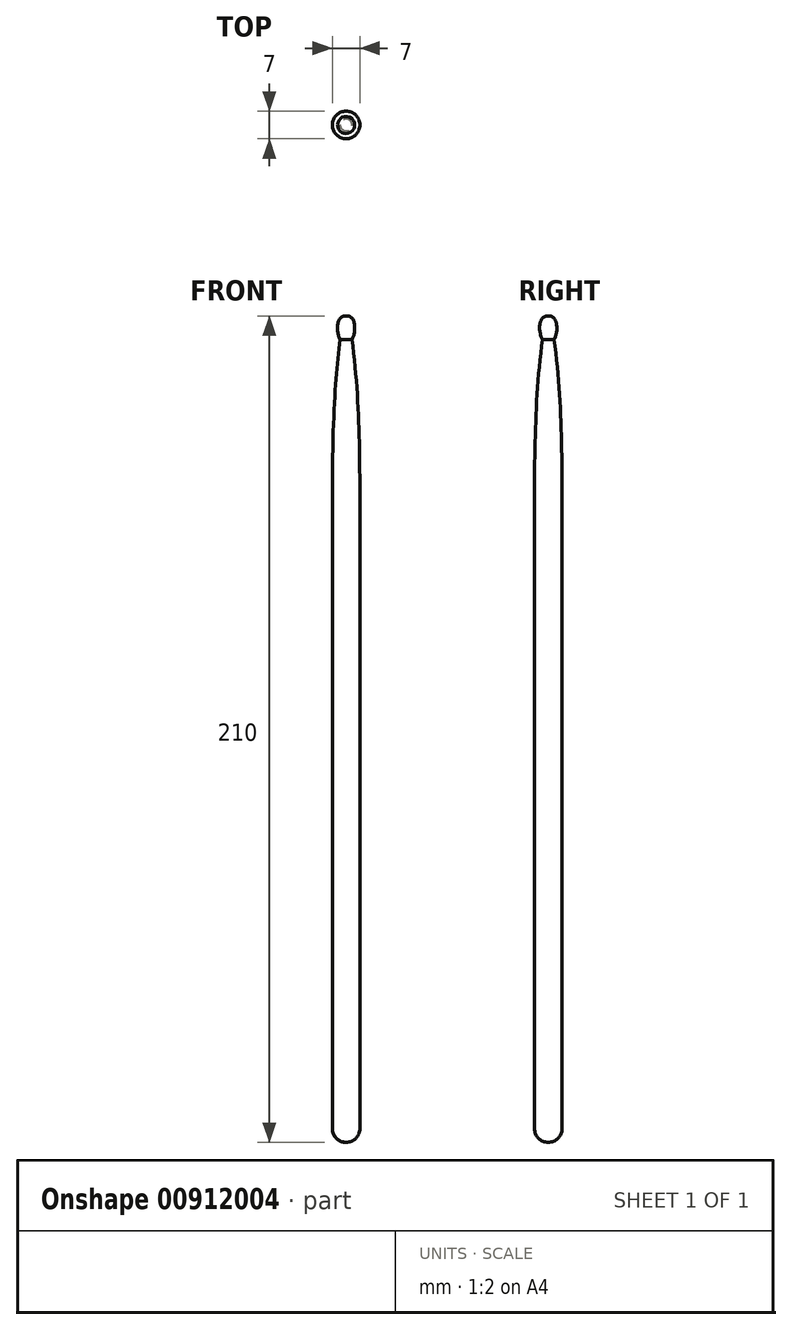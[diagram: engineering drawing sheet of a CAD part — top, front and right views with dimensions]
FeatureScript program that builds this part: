
annotation { "Feature Type Name" : "Feature", "Feature Type Description" : "" }
export const myFeature = defineFeature(function(context is Context, id is Id, definition is map)
    precondition{}
    {
        {
            var Q0;
            Q0=qCreatedBy(makeId("Front.planeOp"),FACE);
            var sketch = newSketch(context, id + "F0", { "sketchPlane" : qUnion([Q0])});
            skLineSegment(sketch, "E0", {"start": v(0, 0) * mm, "end": v(0, 210) * mm});
            skLineSegment(sketch, "E1", {"start": v(-6.22, 210) * mm, "end": v(0, 210) * mm, "construction": true});
            skLineSegment(sketch, "E2", {"start": v(-6.3, 0) * mm, "end": v(0, 0) * mm, "construction": true});
            skLineSegment(sketch, "E3", {"start": v(3.5, 163.85) * mm, "end": v(3.5, 3.5) * mm});
            skArc(sketch, "E4", {"start": v(0, 0) * mm, "mid": v(2.47, 1.03) * mm, "end": v(3.5, 3.5) * mm});
            skFitSpline(sketch, "E5", {"points": [v(0, 210) * mm, v(1.5, 204) * mm], "startDerivative": vector(9.38, 0) * mm, "endDerivative": vector(-2.09, -2.9) * mm});
            skFitSpline(sketch, "E6", {"points": [v(1.5, 204) * mm, v(3.5, 163.85) * mm], "startDerivative": vector(3.4, -26.98) * mm, "endDerivative": vector(0, -64.73) * mm});
            skSolve(sketch);
        }
        {
            var Q0;
            Q0 = qSketchRegion(id + "F0", true);
            var Q1;
            Q1=sQuery(id+"F0.wireOp",EDGE,"E0");
            revolve(context, id + "F1", {"surfaceOperationType" : NewSurfaceOperationType.NEW, "entities" : qUnion([Q0]), "axis" : qUnion([Q1]), "revolveType" : RevolveType.FULL});
        }
    });
